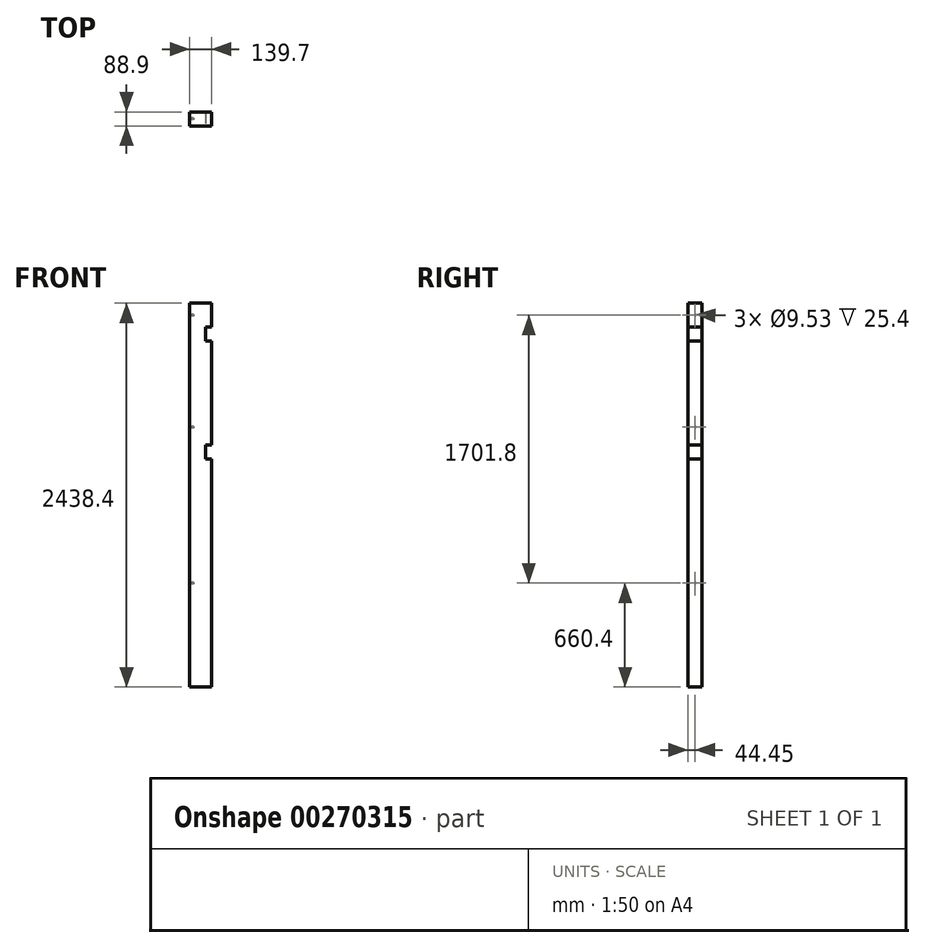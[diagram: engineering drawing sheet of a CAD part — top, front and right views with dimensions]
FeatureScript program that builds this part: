
annotation { "Feature Type Name" : "Feature", "Feature Type Description" : "" }
export const myFeature = defineFeature(function(context is Context, id is Id, definition is map)
    precondition{}
    {
        {
            var Q0;
            Q0=qCreatedBy(makeId("Top.planeOp"),FACE);
            var sketch = newSketch(context, id + "F0", { "sketchPlane" : qUnion([Q0])});
            skLineSegment(sketch, "E0.bottom", {"start": v(69.85, -44.45) * mm, "end": v(-69.85, -44.45) * mm});
            skLineSegment(sketch, "E0.top", {"start": v(69.85, 44.45) * mm, "end": v(-69.85, 44.45) * mm});
            skLineSegment(sketch, "E0.left", {"start": v(69.85, -44.45) * mm, "end": v(69.85, 44.45) * mm});
            skLineSegment(sketch, "E0.right", {"start": v(-69.85, -44.45) * mm, "end": v(-69.85, 44.45) * mm});
            skPoint(sketch, "E0.middle", {"position": v(0, 0) * mm});
            skSolve(sketch);
        }
        {
            var Q0;
            Q0=makeQuery(id+"F0.imprint","IMPRINT",FACE,{"disambiguationData":[TD([[makeQuery(id+"F0.imprint","IMPRINT",EDGE,{"derivedFrom":sQuery(id+"F0.wireOp",EDGE,"E0.bottom")}),-1.0]])]});
            extrude(context, id + "F1", {"entities" : qUnion([Q0]), "endBound" : BoundingType.SYMMETRIC, "depth" : 2438.4 * mm});
        }
        {
            var Q0;
            Q0=makeQuery(id+"F1.opExtrude","SWEPT_FACE",FACE,{"disambiguationData":[OSD([sQuery(id+"F0.wireOp",EDGE,"E0.left")])]});
            var sketch = newSketch(context, id + "F2", { "sketchPlane" : qUnion([Q0])});
            skLineSegment(sketch, "E1.bottom", {"start": v(44.45, 977.9) * mm, "end": v(-44.45, 977.9) * mm});
            skLineSegment(sketch, "E1.top", {"start": v(44.45, 1066.8) * mm, "end": v(-44.45, 1066.8) * mm});
            skLineSegment(sketch, "E1.left", {"start": v(44.45, 977.9) * mm, "end": v(44.45, 1066.8) * mm});
            skLineSegment(sketch, "E1.right", {"start": v(-44.45, 977.9) * mm, "end": v(-44.45, 1066.8) * mm});
            skPoint(sketch, "E1.middle", {"position": v(0, 1022.35) * mm});
            skLineSegment(sketch, "E2.bottom", {"start": v(44.45, 228.6) * mm, "end": v(-44.45, 228.6) * mm});
            skLineSegment(sketch, "E2.top", {"start": v(44.45, 317.5) * mm, "end": v(-44.45, 317.5) * mm});
            skLineSegment(sketch, "E2.left", {"start": v(44.45, 228.6) * mm, "end": v(44.45, 317.5) * mm});
            skLineSegment(sketch, "E2.right", {"start": v(-44.45, 228.6) * mm, "end": v(-44.45, 317.5) * mm});
            skPoint(sketch, "E2.middle", {"position": v(0, 273.05) * mm});
            skSolve(sketch);
        }
        {
            var Q0;
            Q0=qSketchRegion(id+"F2",true);
            extrude(context, id + "F3", {"entities" : qUnion([Q0]), "operationType" : NewBodyOperationType.REMOVE, "oppositeDirection" : true, "depth" : 38.1 * mm});
        }
        {
            var Q0;
            Q0=makeQuery(id+"F1.opExtrude","SWEPT_FACE",FACE,{"disambiguationData":[OSD([sQuery(id+"F0.wireOp",EDGE,"E0.right")])]});
            var sketch = newSketch(context, id + "F4", { "sketchPlane" : qUnion([Q0])});
            skCircle(sketch, "E3", {"center": v(0, -558.8) * mm, "radius": 4.76 * mm});
            skPoint(sketch, "E3.centerSnap0", {"position": v(0, -1219.2) * mm});
            skCircle(sketch, "E4", {"center": v(0, 1143) * mm, "radius": 4.76 * mm});
            skCircle(sketch, "E5", {"center": v(0, 431.8) * mm, "radius": 4.76 * mm});
            skPoint(sketch, "E6", {"position": v(0, -609.6) * mm});
            skSolve(sketch);
        }
        {
            var Q0;
            Q0 = qSketchRegion(id + "F4", true);
            extrude(context, id + "F5", {"entities" : qUnion([Q0]), "operationType" : NewBodyOperationType.REMOVE, "oppositeDirection" : true, "depth" : 25.4 * mm});
        }
    });
